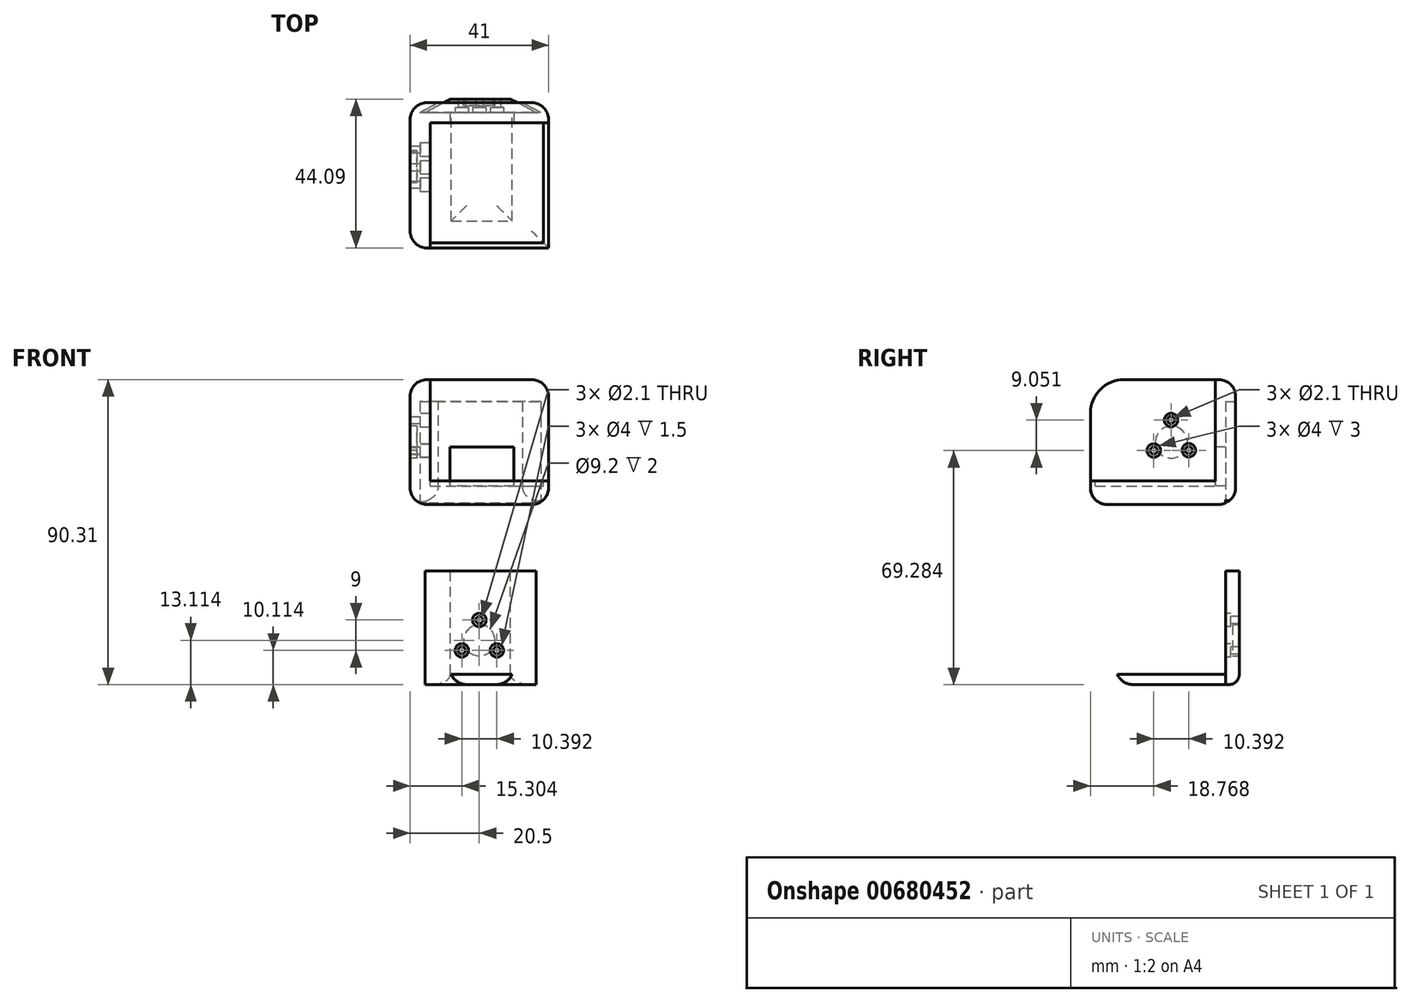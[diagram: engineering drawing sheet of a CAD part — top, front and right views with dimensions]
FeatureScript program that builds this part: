
annotation { "Feature Type Name" : "Feature", "Feature Type Description" : "" }
export const myFeature = defineFeature(function(context is Context, id is Id, definition is map)
    precondition{}
    {
        {
            var Q0;
            Q0=qCreatedBy(makeId("Top.planeOp"),FACE);
            var sketch = newSketch(context, id + "F0", { "sketchPlane" : qUnion([Q0])});
            skLineSegment(sketch, "E0.bottom", {"start": v(20.5, -21.5) * mm, "end": v(-20.5, -21.5) * mm});
            skLineSegment(sketch, "E0.top", {"start": v(20.5, 21.5) * mm, "end": v(-20.5, 21.5) * mm});
            skLineSegment(sketch, "E0.left", {"start": v(20.5, -21.5) * mm, "end": v(20.5, 21.5) * mm});
            skLineSegment(sketch, "E0.right", {"start": v(-20.5, -21.5) * mm, "end": v(-20.5, 21.5) * mm});
            skPoint(sketch, "E0.middle", {"position": v(0, 0) * mm});
            skSolve(sketch);
        }
        {
            var Q0;
            Q0=makeQuery(id+"F0.imprint","IMPRINT",FACE,{"disambiguationData":[TD([[makeQuery(id+"F0.imprint","IMPRINT",EDGE,{"derivedFrom":sQuery(id+"F0.wireOp",EDGE,"E0.bottom")}),-1.0]])]});
            extrude(context, id + "F1", {"entities" : qUnion([Q0]), "depth" : 37 * mm, "offsetDistance" : 25 * mm});
        }
        {
            var Q0;
            Q0=makeQuery(id+"F1.opExtrude","SWEPT_FACE",FACE,{"disambiguationData":[OSD([sQuery(id+"F0.wireOp",EDGE,"E0.left")])]});
            var sketch = newSketch(context, id + "F2", { "sketchPlane" : qUnion([Q0])});
            skLineSegment(sketch, "E1", {"start": v(-21.5, 7) * mm, "end": v(15.5, 7) * mm});
            skLineSegment(sketch, "E2", {"start": v(15.5, 7) * mm, "end": v(15.5, 37) * mm});
            skSolve(sketch);
        }
        {
            var Q0;
            {var subQ0=sQuery(id+"F2.wireOp",EDGE,"E1");Q0=makeQuery(id+"F2.imprint","IMPRINT",FACE,{"disambiguationData":[TD([[makeQuery(id+"F2.imprint","IMPRINT",EDGE,{"derivedFrom":subQ0}),1.0]])]});}
            var Q1;
            Q1=makeQuery(id+"F1.opExtrude","SWEPT_FACE",FACE,{"disambiguationData":[OSD([sQuery(id+"F0.wireOp",EDGE,"E0.right")])]});
            extrude(context, id + "F3", {"entities" : qUnion([Q0]), "operationType" : NewBodyOperationType.REMOVE, "endBound" : BoundingType.UP_TO_SURFACE, "oppositeDirection" : true, "depth" : 25 * mm, "endBoundEntityFace" : qUnion([Q1]), "hasOffset" : true, "offsetDistance" : 6 * mm});
        }
        {
            var Q0;
            Q0=makeQuery(id+"F3.boolean.opBoolean","COPY",FACE,{"derivedFrom":makeQuery(id+"F3.opExtrude","SWEPT_FACE",FACE,{"disambiguationData":[OSD([sQuery(id+"F2.wireOp",EDGE,"E1")])]})});
            var sketch = newSketch(context, id + "F4", { "sketchPlane" : qUnion([Q0])});
            skLineSegment(sketch, "E3", {"start": v(-14.5, -20) * mm, "end": v(19, -20) * mm});
            skLineSegment(sketch, "E4", {"start": v(19, -20) * mm, "end": v(19, 15.5) * mm});
            skSolve(sketch);
        }
        {
            var Q0;
            {var subQ0=sQuery(id+"F4.wireOp",EDGE,"E3");Q0=makeQuery(id+"F4.imprint","IMPRINT",FACE,{"disambiguationData":[TD([[makeQuery(id+"F4.imprint","IMPRINT",EDGE,{"derivedFrom":subQ0}),1.0]])]});}
            extrude(context, id + "F5", {"entities" : qUnion([Q0]), "operationType" : NewBodyOperationType.REMOVE, "oppositeDirection" : true, "depth" : 1.5 * mm, "offsetDistance" : 25 * mm});
        }
        {
            var Q0;
            Q0=makeQuery(id+"F1.opExtrude","CAP_EDGE",EDGE,{"disambiguationData":[OSD([sQuery(id+"F0.wireOp",EDGE,"E0.bottom")])],"isStart":false});
            fillet(context, id + "F6", {"entities" : qUnion([Q0]), "radius" : 10 * mm, "tangentPropagation" : true, "allowEdgeOverflow" : false});
        }
        {
            var Q0;
            Q0=qCreatedBy(makeId("Top.planeOp"),FACE);
            var sketch = newSketch(context, id + "F7", { "sketchPlane" : qUnion([Q0])});
            skLineSegment(sketch, "E5", {"start": v(4.03, 39.3) * mm, "end": v(-15.97, 39.3) * mm});
            skLineSegment(sketch, "E6", {"start": v(-15.97, 39.3) * mm, "end": v(-23.47, 35.3) * mm});
            skLineSegment(sketch, "E7", {"start": v(-23.47, 35.3) * mm, "end": v(11.53, 35.3) * mm});
            skLineSegment(sketch, "E8", {"start": v(11.53, 35.3) * mm, "end": v(4.03, 39.3) * mm});
            skSolve(sketch);
        }
        {
            var Q0;
            Q0=makeQuery(id+"F7.imprint","IMPRINT",FACE,{"disambiguationData":[TD([[makeQuery(id+"F7.imprint","IMPRINT",EDGE,{"derivedFrom":sQuery(id+"F7.wireOp",EDGE,"E5")}),1.0]])]});
            var Q1;
            Q1=makeQuery(id+"F1.opExtrude","CAP_FACE",FACE,{"disambiguationData":[OSD([sQuery(id+"F0.wireOp",EDGE,"E0.bottom"),sQuery(id+"F0.wireOp",EDGE,"E0.top"),sQuery(id+"F0.wireOp",EDGE,"E0.left"),sQuery(id+"F0.wireOp",EDGE,"E0.right")])],"isStart":false});
            extrude(context, id + "F8", {"entities" : qUnion([Q0]), "depth" : 30.7 * mm, "endBoundEntityFace" : qUnion([Q1]), "offsetDistance" : 25 * mm});
        }
        {
            var Q0;
            Q0=makeQuery(id+"F8.opExtrude","SWEPT_BODY",BODY,{"disambiguationData":[OSD([sQuery(id+"F7.wireOp",EDGE,"E5"),sQuery(id+"F7.wireOp",EDGE,"E6"),sQuery(id+"F7.wireOp",EDGE,"E7"),sQuery(id+"F7.wireOp",EDGE,"E8")])]});
            transform(context, id + "F9", {"entities" : qUnion([Q0]), "transformType" : TransformType.TRANSLATION_3D, "dx" : 6.3 * mm, "dy" : -16.7 * mm, "dz" : -0.2 * mm, "makeCopy" : false});
        }
        {
            var Q0;
            Q0=makeQuery(id+"F8.opExtrude","SWEPT_BODY",BODY,{"disambiguationData":[OSD([sQuery(id+"F7.wireOp",EDGE,"E5"),sQuery(id+"F7.wireOp",EDGE,"E6"),sQuery(id+"F7.wireOp",EDGE,"E7"),sQuery(id+"F7.wireOp",EDGE,"E8")])]});
            var Q1;
            Q1=makeQuery(id+"F1.opExtrude","SWEPT_BODY",BODY,{"disambiguationData":[OSD([sQuery(id+"F0.wireOp",EDGE,"E0.bottom"),sQuery(id+"F0.wireOp",EDGE,"E0.top"),sQuery(id+"F0.wireOp",EDGE,"E0.left"),sQuery(id+"F0.wireOp",EDGE,"E0.right")])]});
            var Q2;
            Q2=makeQuery(id+"F8.opExtrude","SWEPT_FACE",FACE,{"disambiguationData":[OSD([sQuery(id+"F7.wireOp",EDGE,"E6")])]});
            var Q3;
            Q3=makeQuery(id+"F8.opExtrude","SWEPT_FACE",FACE,{"disambiguationData":[OSD([sQuery(id+"F7.wireOp",EDGE,"E8")])]});
            booleanBodies(context, id + "F10", {"operationType" : BooleanOperationType.SUBTRACTION, "tools" : qUnion([Q0]), "targets" : qUnion([Q1]), "offset" : true, "entitiesToOffset" : qUnion([Q2, Q3]), "offsetDistance" : 0.2 * mm, "keepTools" : true});
        }
        {
            var Q0;
            Q0=qCreatedBy(makeId("Right.planeOp"),FACE);
            var sketch = newSketch(context, id + "F11", { "sketchPlane" : qUnion([Q0])});
            skLineSegment(sketch, "E9", {"start": v(43.92, 45.33) * mm, "end": v(43.92, -7.77) * mm, "construction": true});
            skSolve(sketch);
        }
        {
            var Q0;
            Q0=makeQuery(id+"F8.opExtrude","SWEPT_BODY",BODY,{"disambiguationData":[OSD([sQuery(id+"F7.wireOp",EDGE,"E5"),sQuery(id+"F7.wireOp",EDGE,"E6"),sQuery(id+"F7.wireOp",EDGE,"E7"),sQuery(id+"F7.wireOp",EDGE,"E8")])]});
            var Q1;
            Q1=sQuery(id+"F11.wireOp",EDGE,"E9");
            transform(context, id + "F12", {"entities" : qUnion([Q0]), "transformType" : TransformType.TRANSLATION_ENTITY, "oppositeDirectionEntity" : false, "transformLine" : qUnion([Q1]), "makeCopy" : false});
        }
        {
            var Q0;
            Q0=makeQuery(id+"F1.opExtrude","CAP_EDGE",EDGE,{"disambiguationData":[OSD([sQuery(id+"F0.wireOp",EDGE,"E0.left")])],"isStart":false});
            fillet(context, id + "F13", {"entities" : qUnion([Q0]), "radius" : 5 * mm, "tangentPropagation" : true, "allowEdgeOverflow" : false});
        }
        {
            var Q0;
            Q0=makeQuery(id+"F1.opExtrude","SWEPT_EDGE",EDGE,{"disambiguationData":[OSD([sQuery(id+"F0.wireOp",EDGE,"E0.top"),sQuery(id+"F0.wireOp",EDGE,"E0.left")])]});
            fillet(context, id + "F14", {"entities" : qUnion([Q0]), "radius" : 5 * mm, "tangentPropagation" : true, "allowEdgeOverflow" : false});
        }
        {
            var Q0;
            Q0=makeQuery(id+"F14.opFillet","BLEND_EDGE",EDGE,{"blendedFrom":[makeQuery(id+"F1.opExtrude","CAP_EDGE",EDGE,{"disambiguationData":[OSD([sQuery(id+"F0.wireOp",EDGE,"E0.top")])],"isStart":false}),makeQuery(id+"F1.opExtrude","SWEPT_FACE",FACE,{"disambiguationData":[OSD([sQuery(id+"F0.wireOp",EDGE,"E0.right")])]})],"blendedInto":[makeQuery(id+"F1.opExtrude","SWEPT_FACE",FACE,{"disambiguationData":[OSD([sQuery(id+"F0.wireOp",EDGE,"E0.right")])]})]});
            var Q1;
            Q1=makeQuery(id+"F1.opExtrude","CAP_EDGE",EDGE,{"disambiguationData":[OSD([sQuery(id+"F0.wireOp",EDGE,"E0.right")])],"isStart":false});
            var Q2;
            Q2=makeQuery(id+"F6.opFillet","BLEND_EDGE",EDGE,{"blendedFrom":[makeQuery(id+"F1.opExtrude","CAP_EDGE",EDGE,{"disambiguationData":[OSD([sQuery(id+"F0.wireOp",EDGE,"E0.bottom")])],"isStart":false}),makeQuery(id+"F1.opExtrude","SWEPT_FACE",FACE,{"disambiguationData":[OSD([sQuery(id+"F0.wireOp",EDGE,"E0.right")])]})],"blendedInto":[makeQuery(id+"F1.opExtrude","SWEPT_FACE",FACE,{"disambiguationData":[OSD([sQuery(id+"F0.wireOp",EDGE,"E0.right")])]})]});
            var Q3;
            Q3=makeQuery(id+"F1.opExtrude","SWEPT_EDGE",EDGE,{"disambiguationData":[OSD([sQuery(id+"F0.wireOp",EDGE,"E0.bottom"),sQuery(id+"F0.wireOp",EDGE,"E0.right")])]});
            fillet(context, id + "F15", {"entities" : qUnion([Q0, Q1, Q2, Q3]), "radius" : 5 * mm, "tangentPropagation" : true, "allowEdgeOverflow" : false});
        }
        {
            var Q0;
            {var subQ0=sQuery(id+"F2.wireOp",EDGE,"E2");Q0=makeQuery(id+"F5.boolean.opBoolean","MERGE",FACE,{"derivedFrom":[makeQuery(id+"F3.boolean.opBoolean","COPY",FACE,{"derivedFrom":makeQuery(id+"F3.opExtrude","SWEPT_FACE",FACE,{"disambiguationData":[OSD([subQ0])]})})],"fromTools":[makeQuery(id+"F5.opExtrude","SWEPT_FACE",FACE,{"disambiguationData":[OSD([sQuery(id+"F2.wireOp",EDGE,"E1"),subQ0])]})]});}
            var sketch = newSketch(context, id + "F16", { "sketchPlane" : qUnion([Q0])});
            skLineSegment(sketch, "E10", {"start": v(-8.7, 5.5) * mm, "end": v(-8.7, 17.07) * mm});
            skLineSegment(sketch, "E11", {"start": v(-8.7, 17.07) * mm, "end": v(10.17, 17.07) * mm});
            skLineSegment(sketch, "E12", {"start": v(10.17, 17.07) * mm, "end": v(10.17, 5.5) * mm});
            skSolve(sketch);
        }
        {
            var Q0;
            {var subQ0=sQuery(id+"F16.wireOp",EDGE,"E10");Q0=makeQuery(id+"F16.imprint","IMPRINT",FACE,{"disambiguationData":[TD([[makeQuery(id+"F16.imprint","IMPRINT",EDGE,{"derivedFrom":subQ0}),-1.0]])]});}
            var Q1;
            Q1=makeQuery(id+"F10.opBoolean","COPY",FACE,{"derivedFrom":makeQuery(id+"F8.opExtrude","SWEPT_FACE",FACE,{"disambiguationData":[OSD([sQuery(id+"F7.wireOp",EDGE,"E7")])]})});
            extrude(context, id + "F17", {"entities" : qUnion([Q0]), "operationType" : NewBodyOperationType.REMOVE, "oppositeDirection" : true, "depth" : 25 * mm, "endBoundEntityFace" : qUnion([Q1]), "offsetDistance" : 25 * mm});
        }
        {
            var Q0;
            Q0=makeQuery(id+"F8.opExtrude","SWEPT_FACE",FACE,{"disambiguationData":[OSD([sQuery(id+"F7.wireOp",EDGE,"E7")])]});
            var sketch = newSketch(context, id + "F18", { "sketchPlane" : qUnion([Q0])});
            skLineSegment(sketch, "E13", {"start": v(-8.32, -53.3) * mm, "end": v(-8.32, -50.3) * mm});
            skLineSegment(sketch, "E14", {"start": v(-8.32, -50.3) * mm, "end": v(9.68, -50.3) * mm});
            skLineSegment(sketch, "E15", {"start": v(9.68, -50.3) * mm, "end": v(9.68, -53.3) * mm});
            skSolve(sketch);
        }
        {
            var Q0;
            {var subQ0=sQuery(id+"F18.wireOp",EDGE,"E13");Q0=makeQuery(id+"F18.imprint","IMPRINT",FACE,{"disambiguationData":[TD([[makeQuery(id+"F18.imprint","IMPRINT",EDGE,{"derivedFrom":subQ0}),-1.0]])]});}
            extrude(context, id + "F19", {"entities" : qUnion([Q0]), "operationType" : NewBodyOperationType.ADD, "depth" : 32.1 * mm, "offsetDistance" : 25 * mm});
        }
        {
            var Q0;
            Q0=makeQuery(id+"F19.opExtrude","CAP_EDGE",EDGE,{"disambiguationData":[OSD([sQuery(id+"F7.wireOp",EDGE,"E7")])],"isStart":false});
            fillet(context, id + "F20", {"entities" : qUnion([Q0]), "radius" : 5 * mm, "tangentPropagation" : true, "allowEdgeOverflow" : false});
        }
        {
            var Q0;
            Q0=makeQuery(id+"F8.opExtrude","CAP_FACE",FACE,{"disambiguationData":[OSD([sQuery(id+"F7.wireOp",EDGE,"E5"),sQuery(id+"F7.wireOp",EDGE,"E6"),sQuery(id+"F7.wireOp",EDGE,"E7"),sQuery(id+"F7.wireOp",EDGE,"E8")])],"isStart":false});
            extrude(context, id + "F21", {"entities" : qUnion([Q0]), "operationType" : NewBodyOperationType.ADD, "depth" : 3 * mm, "offsetDistance" : 25 * mm});
        }
        {
            var Q0;
            Q0=makeQuery(id+"F8.opExtrude","CAP_EDGE",EDGE,{"disambiguationData":[OSD([sQuery(id+"F7.wireOp",EDGE,"E5")])],"isStart":true});
            fillet(context, id + "F22", {"entities" : qUnion([Q0]), "radius" : 3 * mm, "tangentPropagation" : true, "allowEdgeOverflow" : false});
        }
        {
            var Q0;
            Q0=makeQuery(id+"F19.opExtrude","SWEPT_EDGE",EDGE,{"disambiguationData":[OSD([sQuery(id+"F7.wireOp",EDGE,"E7"),sQuery(id+"F18.wireOp",EDGE,"E13")])]});
            var Q1;
            Q1=makeQuery(id+"F19.opExtrude","SWEPT_EDGE",EDGE,{"disambiguationData":[OSD([sQuery(id+"F7.wireOp",EDGE,"E7"),sQuery(id+"F18.wireOp",EDGE,"E15")])]});
            fillet(context, id + "F23", {"entities" : qUnion([Q0, Q1]), "radius" : 5 * mm, "tangentPropagation" : true, "allowEdgeOverflow" : false});
        }
        {
            var Q0;
            {var subQ0=sQuery(id+"F7.wireOp",EDGE,"E7");Q0=makeQuery(id+"F21.boolean.opBoolean","MERGE",FACE,{"derivedFrom":[makeQuery(id+"F8.opExtrude","SWEPT_FACE",FACE,{"disambiguationData":[OSD([subQ0])]}),makeQuery(id+"F21.opExtrude","SWEPT_FACE",FACE,{"disambiguationData":[OSD([subQ0])]})]});}
            var sketch = newSketch(context, id + "F24", { "sketchPlane" : qUnion([Q0])});
            skCircle(sketch, "E16", {"center": v(0, -40.18) * mm, "radius": 4.5 * mm});
            skSolve(sketch);
        }
        {
            var Q0;
            Q0=makeQuery(id+"F1.opExtrude","CAP_FACE",FACE,{"disambiguationData":[OSD([sQuery(id+"F0.wireOp",EDGE,"E0.bottom"),sQuery(id+"F0.wireOp",EDGE,"E0.top"),sQuery(id+"F0.wireOp",EDGE,"E0.left"),sQuery(id+"F0.wireOp",EDGE,"E0.right")])],"isStart":true});
            var sketch = newSketch(context, id + "F25", { "sketchPlane" : qUnion([Q0])});
            skLineSegment(sketch, "E17", {"start": v(0, 0) * mm, "end": v(0, 10) * mm, "construction": true});
            skLineSegment(sketch, "E18", {"start": v(0, 0) * mm, "end": v(0, -10) * mm, "construction": true});
            skLineSegment(sketch, "E19", {"start": v(0, 10) * mm, "end": v(20.5, 10) * mm});
            skLineSegment(sketch, "E20", {"start": v(0, 10) * mm, "end": v(-20.5, 10) * mm});
            skLineSegment(sketch, "E21", {"start": v(0, -10) * mm, "end": v(20.5, -10) * mm});
            skLineSegment(sketch, "E22", {"start": v(0, -10) * mm, "end": v(-20.5, -10) * mm});
            skSolve(sketch);
        }
        {
            var Q0;
            Q0=makeQuery(id+"F1.opExtrude","CAP_EDGE",EDGE,{"disambiguationData":[OSD([sQuery(id+"F0.wireOp",EDGE,"E0.bottom")])],"isStart":true});
            var Q1;
            {var subQ0=sQuery(id+"F0.wireOp",EDGE,"E0.right");var subQ1=sQuery(id+"F0.wireOp",EDGE,"E0.bottom");Q1=makeQuery(id+"F15.opFillet","BLEND_EDGE",EDGE,{"blendedFrom":[makeQuery(id+"F1.opExtrude","SWEPT_EDGE",EDGE,{"disambiguationData":[OSD([subQ1,subQ0])]}),makeQuery(id+"F1.opExtrude","CAP_FACE",FACE,{"disambiguationData":[OSD([subQ1,sQuery(id+"F0.wireOp",EDGE,"E0.top"),sQuery(id+"F0.wireOp",EDGE,"E0.left"),subQ0])],"isStart":true})],"blendedInto":[makeQuery(id+"F1.opExtrude","CAP_FACE",FACE,{"disambiguationData":[OSD([subQ1,sQuery(id+"F0.wireOp",EDGE,"E0.top"),sQuery(id+"F0.wireOp",EDGE,"E0.left"),subQ0])],"isStart":true})]});}
            var Q2;
            {var subQ0=sQuery(id+"F0.wireOp",EDGE,"E0.right");var subQ1=sQuery(id+"F0.wireOp",EDGE,"E0.top");Q2=makeQuery(id+"F15.opFillet","BLEND_EDGE",EDGE,{"blendedFrom":[makeQuery(id+"F1.opExtrude","SWEPT_EDGE",EDGE,{"disambiguationData":[OSD([subQ1,subQ0])]}),makeQuery(id+"F1.opExtrude","CAP_FACE",FACE,{"disambiguationData":[OSD([sQuery(id+"F0.wireOp",EDGE,"E0.bottom"),subQ1,sQuery(id+"F0.wireOp",EDGE,"E0.left"),subQ0])],"isStart":true})],"blendedInto":[makeQuery(id+"F1.opExtrude","CAP_FACE",FACE,{"disambiguationData":[OSD([sQuery(id+"F0.wireOp",EDGE,"E0.bottom"),subQ1,sQuery(id+"F0.wireOp",EDGE,"E0.left"),subQ0])],"isStart":true})]});}
            var Q3;
            {var subQ0=sQuery(id+"F0.wireOp",EDGE,"E0.bottom");var subQ1=sQuery(id+"F0.wireOp",EDGE,"E0.left");Q3=makeQuery(id+"FPZz39PcZ6kap4B_2.boolean.opBoolean","SPLIT",EDGE,{"disambiguationData":[TD([makeQuery(id+"F1.opExtrude","SWEPT_FACE",FACE,{"disambiguationData":[OSD([subQ0])]})])],"derivedFrom":makeQuery(id+"F1.opExtrude","CAP_EDGE",EDGE,{"disambiguationData":[OSD([subQ1])],"isStart":true})});}
            var Q4;
            {var subQ0=sQuery(id+"F0.wireOp",EDGE,"E0.left");Q4=makeQuery(id+"FPZz39PcZ6kap4B_2.boolean.opBoolean","SPLIT",EDGE,{"disambiguationData":[TD([makeQuery(id+"FPZz39PcZ6kap4B_2.opExtrude","SWEPT_FACE",FACE,{"disambiguationData":[OSD([sQuery(id+"F25.wireOp",EDGE,"E21"),sQuery(id+"F25.wireOp",EDGE,"E22")])]})])],"derivedFrom":makeQuery(id+"F1.opExtrude","CAP_EDGE",EDGE,{"disambiguationData":[OSD([subQ0])],"isStart":true})});}
            fillet(context, id + "F26", {"entities" : qUnion([Q0, Q1, Q2, Q3, Q4]), "radius" : 5 * mm, "tangentPropagation" : true, "allowEdgeOverflow" : false});
        }
        {
            var Q0;
            Q0=makeQuery(id+"F21.opExtrude","CAP_FACE",FACE,{"disambiguationData":[OSD([sQuery(id+"F7.wireOp",EDGE,"E5"),sQuery(id+"F7.wireOp",EDGE,"E6"),sQuery(id+"F7.wireOp",EDGE,"E7"),sQuery(id+"F7.wireOp",EDGE,"E8")])],"isStart":false});
            var sketch = newSketch(context, id + "F27", { "sketchPlane" : qUnion([Q0])});
            skLineSegment(sketch, "E23", {"start": v(16.77, 18.6) * mm, "end": v(9.27, 22.6) * mm});
            skLineSegment(sketch, "E24", {"start": v(-16.1, 18.6) * mm, "end": v(-8.6, 22.6) * mm});
            skSolve(sketch);
        }
        {
            var Q0;
            {var subQ0=sQuery(id+"F27.wireOp",EDGE,"E24");Q0=makeQuery(id+"F27.imprint","IMPRINT",FACE,{"disambiguationData":[TD([[makeQuery(id+"F27.imprint","IMPRINT",EDGE,{"derivedFrom":subQ0}),1.0]])]});}
            var Q1;
            {var subQ0=sQuery(id+"F27.wireOp",EDGE,"E23");Q1=makeQuery(id+"F27.imprint","IMPRINT",FACE,{"disambiguationData":[TD([[makeQuery(id+"F27.imprint","IMPRINT",EDGE,{"derivedFrom":subQ0}),-1.0]])]});}
            extrude(context, id + "F28", {"entities" : qUnion([Q0, Q1]), "operationType" : NewBodyOperationType.REMOVE, "oppositeDirection" : true, "depth" : 35 * mm, "offsetDistance" : 25 * mm});
        }
        {
            var Q0;
            {var subQ0=sQuery(id+"F7.wireOp",EDGE,"E5");Q0=makeQuery(id+"F21.boolean.opBoolean","MERGE",FACE,{"derivedFrom":[makeQuery(id+"F8.opExtrude","SWEPT_FACE",FACE,{"disambiguationData":[OSD([subQ0])]}),makeQuery(id+"F21.opExtrude","SWEPT_FACE",FACE,{"disambiguationData":[OSD([subQ0])]})]});}
            var sketch = newSketch(context, id + "F29", { "sketchPlane" : qUnion([Q0])});
            skCircle(sketch, "E25", {"center": v(0, -40.2) * mm, "radius": 4.6 * mm});
            skSolve(sketch);
        }
        {
            var Q0;
            Q0=makeQuery(id+"F29.imprint","IMPRINT",FACE,{"disambiguationData":[TD([[makeQuery(id+"F29.imprint","IMPRINT",EDGE,{"derivedFrom":sQuery(id+"F29.wireOp",EDGE,"E25")}),1.0]])]});
            extrude(context, id + "F30", {"entities" : qUnion([Q0]), "operationType" : NewBodyOperationType.REMOVE, "oppositeDirection" : true, "depth" : 2 * mm, "offsetDistance" : 25 * mm});
        }
        {
            var Q0;
            Q0=makeQuery(id+"F24.imprint","IMPRINT",FACE,{"disambiguationData":[TD([[makeQuery(id+"F24.imprint","IMPRINT",EDGE,{"derivedFrom":sQuery(id+"F24.wireOp",EDGE,"E16")}),1.0]])]});
            var sketch = newSketch(context, id + "F31", { "sketchPlane" : qUnion([Q0])});
            skCircle(sketch, "E26", {"center": v(0, -40.2) * mm, "radius": 6 * mm, "construction": true});
            skLineSegment(sketch, "E27", {"start": v(0, -34.2) * mm, "end": v(0, -40.2) * mm, "construction": true});
            skLineSegment(sketch, "E28", {"start": v(0, -40.2) * mm, "end": v(5.2, -43.2) * mm, "construction": true});
            skLineSegment(sketch, "E29", {"start": v(5.2, -43.2) * mm, "end": v(0, -40.2) * mm, "construction": true});
            skLineSegment(sketch, "E30", {"start": v(0, -40.2) * mm, "end": v(-5.2, -43.2) * mm, "construction": true});
            skPoint(sketch, "E31", {"position": v(0, -34.2) * mm});
            skPoint(sketch, "E32", {"position": v(5.2, -43.2) * mm});
            skPoint(sketch, "E33", {"position": v(-5.2, -43.2) * mm});
            skSolve(sketch);
        }
        {
            var Q0;
            Q0=sQuery(id+"F31.wireOp",VERTEX,"E31");
            var Q1;
            Q1=sQuery(id+"F31.wireOp",VERTEX,"E32");
            var Q2;
            Q2=sQuery(id+"F31.wireOp",VERTEX,"E33");
            var Q3;
            Q3=makeQuery(id+"F8.opExtrude","SWEPT_BODY",BODY,{"disambiguationData":[OSD([sQuery(id+"F7.wireOp",EDGE,"E5"),sQuery(id+"F7.wireOp",EDGE,"E6"),sQuery(id+"F7.wireOp",EDGE,"E7"),sQuery(id+"F7.wireOp",EDGE,"E8")])]});
            hole(context, id + "F32", {"style" : HoleStyle.C_BORE, "endStyle" : HoleEndStyle.THROUGH, "holeDiameter" : 2.1 * mm, "cBoreDiameter" : 4 * mm, "cBoreDepth" : 1.5 * mm, "majorDiameter" : 5 * mm, "isTappedThrough" : true, "tappedDepth" : 12 * mm, "tapClearance" : 3, "locations" : qUnion([Q0, Q1, Q2]), "scope" : qUnion([Q3])});
        }
        {
            var Q0;
            Q0=makeQuery(id+"F1.opExtrude","SWEPT_FACE",FACE,{"disambiguationData":[OSD([sQuery(id+"F0.wireOp",EDGE,"E0.right")])]});
            var sketch = newSketch(context, id + "F33", { "sketchPlane" : qUnion([Q0])});
            skLineSegment(sketch, "E34", {"start": v(-16.5, 18.5) * mm, "end": v(16.5, 18.5) * mm, "construction": true});
            skLineSegment(sketch, "E35", {"start": v(-2.5, 32) * mm, "end": v(-2.5, 5) * mm, "construction": true});
            skCircle(sketch, "E36", {"center": v(-2.5, 18.5) * mm, "radius": 4.75 * mm});
            skSolve(sketch);
        }
        {
            var Q0;
            Q0=makeQuery(id+"F33.imprint","IMPRINT",FACE,{"disambiguationData":[TD([[makeQuery(id+"F33.imprint","IMPRINT",EDGE,{"derivedFrom":sQuery(id+"F33.wireOp",EDGE,"E36")}),1.0]])]});
            extrude(context, id + "F34", {"entities" : qUnion([Q0]), "operationType" : NewBodyOperationType.REMOVE, "oppositeDirection" : true, "depth" : 2 * mm, "offsetDistance" : 25 * mm});
        }
        {
            var Q0;
            {var subQ0=sQuery(id+"F2.wireOp",EDGE,"E1");Q0=makeQuery(id+"F5.boolean.opBoolean","MERGE",FACE,{"derivedFrom":[makeQuery(id+"F3.boolean.opBoolean","COPY",FACE,{"derivedFrom":makeQuery(id+"F3.opExtrude","CAP_FACE",FACE,{"disambiguationData":[OSD([sQuery(id+"F0.wireOp",EDGE,"E0.bottom"),sQuery(id+"F0.wireOp",EDGE,"E0.left"),subQ0,sQuery(id+"F2.wireOp",EDGE,"E2")])],"isStart":false})})],"fromTools":[makeQuery(id+"F5.opExtrude","SWEPT_FACE",FACE,{"disambiguationData":[OSD([subQ0])]})]});}
            var sketch = newSketch(context, id + "F35", { "sketchPlane" : qUnion([Q0])});
            skCircle(sketch, "E37", {"center": v(2.43, 19.03) * mm, "radius": 6 * mm, "construction": true});
            skLineSegment(sketch, "E38", {"start": v(2.37, 25.03) * mm, "end": v(2.43, 19.03) * mm, "construction": true});
            skLineSegment(sketch, "E39", {"start": v(2.43, 19.03) * mm, "end": v(7.66, 16.08) * mm, "construction": true});
            skLineSegment(sketch, "E40", {"start": v(2.43, 19.03) * mm, "end": v(-2.73, 15.97) * mm, "construction": true});
            skPoint(sketch, "E41", {"position": v(2.37, 25.03) * mm});
            skPoint(sketch, "E42", {"position": v(7.66, 16.08) * mm});
            skPoint(sketch, "E43", {"position": v(-2.73, 15.97) * mm});
            skSolve(sketch);
        }
        {
            var Q0;
            Q0=sQuery(id+"F35.wireOp",VERTEX,"E41");
            var Q1;
            Q1=sQuery(id+"F35.wireOp",VERTEX,"E42");
            var Q2;
            Q2=sQuery(id+"F35.wireOp",VERTEX,"E43");
            var Q3;
            Q3=makeQuery(id+"F1.opExtrude","SWEPT_BODY",BODY,{"disambiguationData":[OSD([sQuery(id+"F0.wireOp",EDGE,"E0.bottom"),sQuery(id+"F0.wireOp",EDGE,"E0.top"),sQuery(id+"F0.wireOp",EDGE,"E0.left"),sQuery(id+"F0.wireOp",EDGE,"E0.right")])]});
            hole(context, id + "F36", {"style" : HoleStyle.C_BORE, "endStyle" : HoleEndStyle.THROUGH, "holeDiameter" : 2.1 * mm, "cBoreDiameter" : 4 * mm, "cBoreDepth" : 3 * mm, "majorDiameter" : 5 * mm, "isTappedThrough" : true, "tappedDepth" : 12 * mm, "tapClearance" : 3, "locations" : qUnion([Q0, Q1, Q2]), "scope" : qUnion([Q3])});
        }
    });
